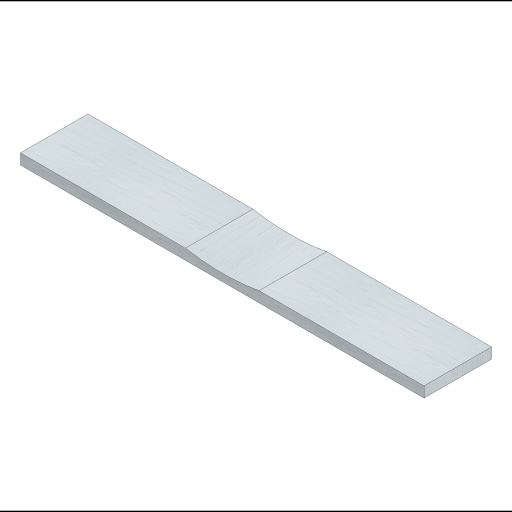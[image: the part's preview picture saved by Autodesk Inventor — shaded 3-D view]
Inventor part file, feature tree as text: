
AUTODESK INVENTOR PART (.ipt)
format: ipt  version: 2023 (Build 270158000, 158)  size: 163,840 bytes
history: native  units: in
note: dims shown in document units (in); Inventor stores cm internally (conversion verified against a paired STEP export)
features: extrude x2, sketch x2
ambient origin geometry x8: Origin, YZ Plane, XZ Plane, XY Plane, X Axis, Y Axis, Z Axis, Center Point
bodies: Solid1 (feature_tree)
feature tree (4):
  extrude  "Extrusion1"  Depth=0.47in
  extrude  "Extrusion2"  Depth=3.0in
  sketch  "Sketch1"  dims[d0=17.9375in d1=0.47in]
  sketch  "Sketch2"  dims[d2=3.0in d3=0.0in d6=8.969in d7=8.85in d8=18.0in d9=0.0in d10=0.0in]
